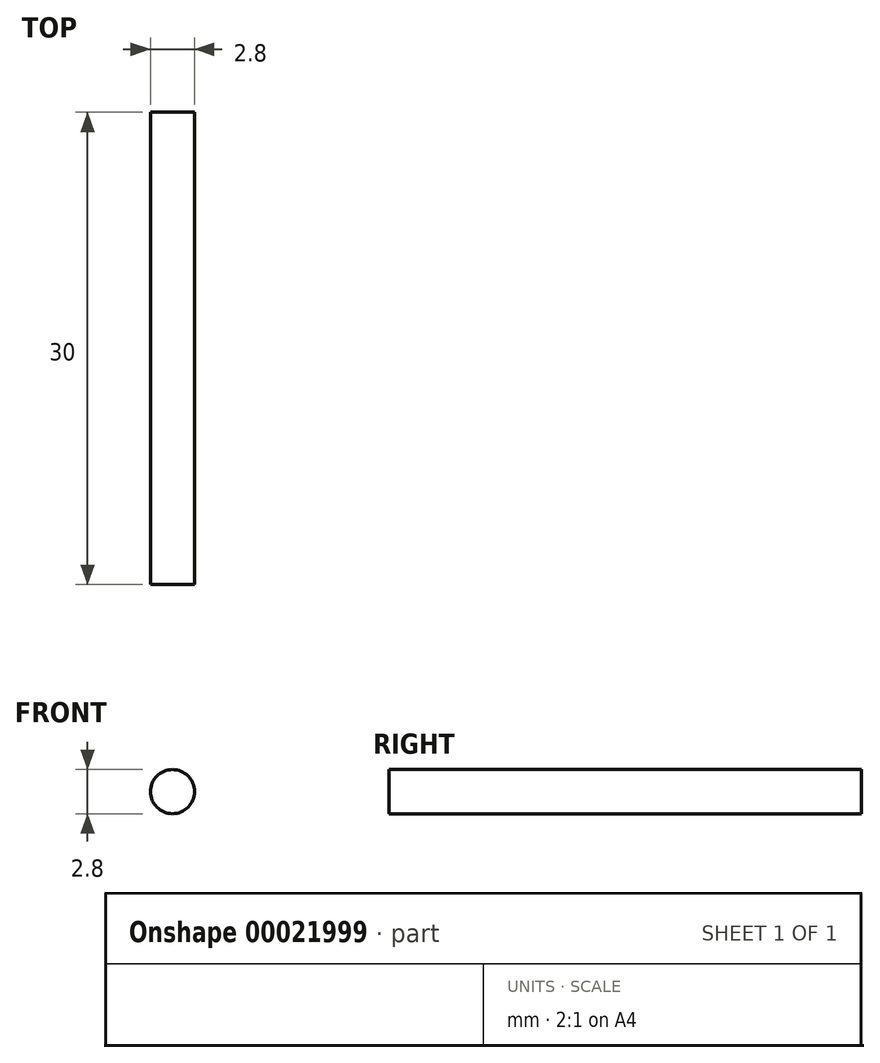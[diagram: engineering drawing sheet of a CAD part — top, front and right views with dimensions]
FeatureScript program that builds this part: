
annotation { "Feature Type Name" : "Feature", "Feature Type Description" : "" }
export const myFeature = defineFeature(function(context is Context, id is Id, definition is map)
    precondition{}
    {
        {
            var Q0;
            Q0=qCreatedBy(makeId("Front.planeOp"),FACE);
            var sketch = newSketch(context, id + "F0", { "sketchPlane" : qUnion([Q0])});
            skCircle(sketch, "E0", {"center": v(0, 0) * mm, "radius": 1.4 * mm});
            skSolve(sketch);
        }
        {
            var Q0;
            Q0 = qSketchRegion(id + "F0", true);
            extrude(context, id + "F1", {"entities" : qUnion([Q0]), "depth" : 30 * mm});
        }
    });
